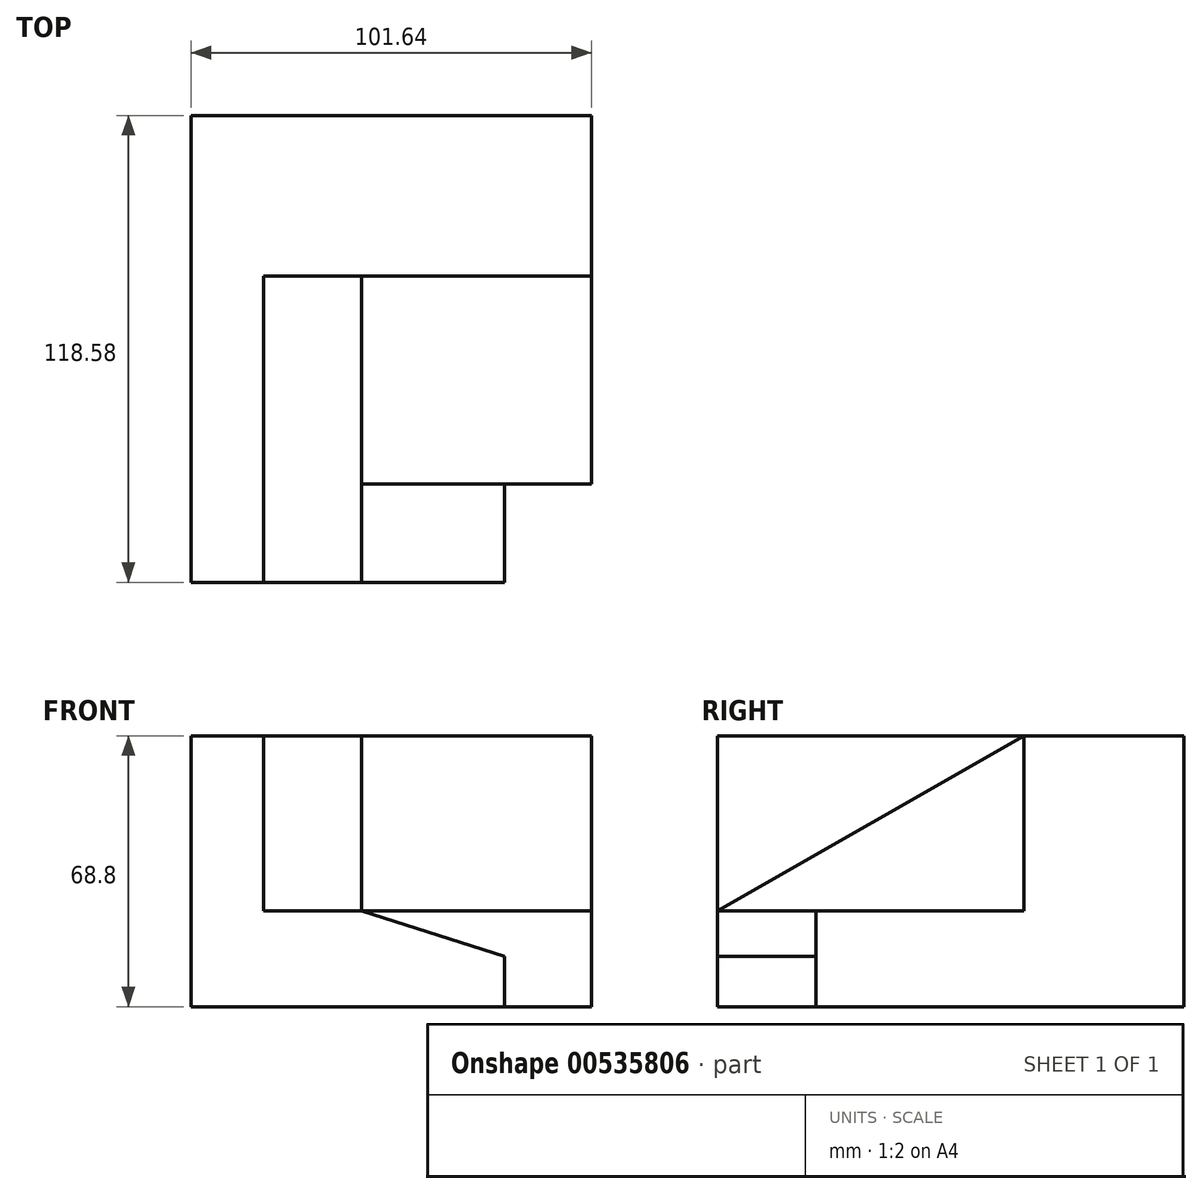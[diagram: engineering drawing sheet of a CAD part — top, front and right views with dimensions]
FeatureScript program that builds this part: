
annotation { "Feature Type Name" : "Feature", "Feature Type Description" : "" }
export const myFeature = defineFeature(function(context is Context, id is Id, definition is map)
    precondition{}
    {
        {
            var Q0;
            Q0=qCreatedBy(makeId("Top.planeOp"),FACE);
            var sketch = newSketch(context, id + "F0", { "sketchPlane" : qUnion([Q0])});
            skLineSegment(sketch, "E0.bottom", {"start": v(50.82, 59.3) * mm, "end": v(-50.82, 59.3) * mm});
            skLineSegment(sketch, "E0.top", {"start": v(-32.5, -59.3) * mm, "end": v(-50.82, -59.3) * mm});
            skLineSegment(sketch, "E0.left", {"start": v(50.82, 59.3) * mm, "end": v(50.82, 18.54) * mm});
            skLineSegment(sketch, "E0.right", {"start": v(-50.82, 59.3) * mm, "end": v(-50.82, -59.3) * mm});
            skPoint(sketch, "E0.middle", {"position": v(0, 0) * mm});
            skLineSegment(sketch, "E1.top", {"start": v(50.82, 18.54) * mm, "end": v(-32.5, 18.54) * mm});
            skLineSegment(sketch, "E1.right", {"start": v(-32.5, -59.3) * mm, "end": v(-32.5, 18.54) * mm});
            skSolve(sketch);
        }
        {
            var Q0;
            Q0=makeQuery(id+"F0.imprint","IMPRINT",FACE,{"disambiguationData":[TD([[makeQuery(id+"F0.imprint","IMPRINT",EDGE,{"derivedFrom":sQuery(id+"F0.wireOp",EDGE,"E0.bottom")}),1.0]])]});
            extrude(context, id + "F1", {"entities" : qUnion([Q0]), "endBound" : BoundingType.SYMMETRIC, "depth" : 68.8 * mm, "offsetDistance" : 25 * mm});
        }
        {
            var Q0;
            Q0=makeQuery(id+"F1.opExtrude","CAP_FACE",FACE,{"disambiguationData":[OSD([sQuery(id+"F0.wireOp",EDGE,"E0.bottom"),sQuery(id+"F0.wireOp",EDGE,"E0.top"),sQuery(id+"F0.wireOp",EDGE,"E0.left"),sQuery(id+"F0.wireOp",EDGE,"E0.right"),sQuery(id+"F0.wireOp",EDGE,"E1.top"),sQuery(id+"F0.wireOp",EDGE,"E1.right")])],"isStart":true});
            var sketch = newSketch(context, id + "F2", { "sketchPlane" : qUnion([Q0])});
            skPoint(sketch, "E2.oppositeSnap0", {"position": v(-41.66, 59.3) * mm});
            skLineSegment(sketch, "E2.bottom", {"start": v(-32.5, -18.54) * mm, "end": v(50.82, -18.54) * mm});
            skLineSegment(sketch, "E2.top", {"start": v(-32.5, 59.3) * mm, "end": v(50.82, 59.3) * mm});
            skLineSegment(sketch, "E2.left", {"start": v(-32.5, -18.54) * mm, "end": v(-32.5, 59.3) * mm});
            skLineSegment(sketch, "E2.right", {"start": v(50.82, -18.54) * mm, "end": v(50.82, 59.3) * mm});
            skSolve(sketch);
        }
        {
            var Q0;
            Q0=makeQuery(id+"F2.imprint","IMPRINT",FACE,{"disambiguationData":[TD([[makeQuery(id+"F2.imprint","IMPRINT",EDGE,{"derivedFrom":sQuery(id+"F2.wireOp",EDGE,"E2.bottom")}),-1.0]])]});
            extrude(context, id + "F3", {"entities" : qUnion([Q0]), "operationType" : NewBodyOperationType.ADD, "oppositeDirection" : true, "depth" : 24.3 * mm, "offsetDistance" : 25 * mm});
        }
        {
            var Q0;
            Q0=makeQuery(id+"F1.opExtrude","SWEPT_FACE",FACE,{"disambiguationData":[OSD([sQuery(id+"F0.wireOp",EDGE,"E1.right")])]});
            var sketch = newSketch(context, id + "F4", { "sketchPlane" : qUnion([Q0])});
            skLineSegment(sketch, "E3", {"start": v(-59.3, -10.1) * mm, "end": v(18.54, 34.4) * mm});
            skLineSegment(sketch, "E4", {"start": v(18.54, 34.4) * mm, "end": v(18.54, -10.1) * mm});
            skLineSegment(sketch, "E5", {"start": v(18.54, -10.1) * mm, "end": v(-59.3, -10.1) * mm});
            skSolve(sketch);
        }
        {
            var Q0;
            Q0=makeQuery(id+"F4.imprint","IMPRINT",FACE,{"disambiguationData":[TD([[makeQuery(id+"F4.imprint","IMPRINT",EDGE,{"derivedFrom":sQuery(id+"F4.wireOp",EDGE,"E3")}),-1.0]])]});
            extrude(context, id + "F5", {"entities" : qUnion([Q0]), "operationType" : NewBodyOperationType.ADD, "depth" : 25 * mm, "offsetDistance" : 25 * mm});
        }
        {
            var Q0;
            Q0=makeQuery(id+"F3.boolean.opBoolean","MERGE",FACE,{"derivedFrom":[makeQuery(id+"F1.opExtrude","SWEPT_FACE",FACE,{"disambiguationData":[OSD([sQuery(id+"F0.wireOp",EDGE,"E0.top")])]}),makeQuery(id+"F3.opExtrude","SWEPT_FACE",FACE,{"disambiguationData":[OSD([sQuery(id+"F2.wireOp",EDGE,"E2.top")])]})]});
            var sketch = newSketch(context, id + "F6", { "sketchPlane" : qUnion([Q0])});
            skLineSegment(sketch, "E6", {"start": v(-7.5, -10.1) * mm, "end": v(28.69, -21.58) * mm});
            skLineSegment(sketch, "E7", {"start": v(28.69, -21.58) * mm, "end": v(28.69, -34.4) * mm});
            skLineSegment(sketch, "E8", {"start": v(28.69, -34.4) * mm, "end": v(50.82, -34.4) * mm});
            skLineSegment(sketch, "E9", {"start": v(50.82, -34.4) * mm, "end": v(50.82, -10.1) * mm});
            skLineSegment(sketch, "E10", {"start": v(50.82, -10.1) * mm, "end": v(-7.5, -10.1) * mm});
            skSolve(sketch);
        }
        {
            var Q0;
            Q0=makeQuery(id+"F6.imprint","IMPRINT",FACE,{"disambiguationData":[TD([[makeQuery(id+"F6.imprint","IMPRINT",EDGE,{"derivedFrom":sQuery(id+"F6.wireOp",EDGE,"E6")}),1.0]])]});
            extrude(context, id + "F7", {"entities" : qUnion([Q0]), "operationType" : NewBodyOperationType.REMOVE, "oppositeDirection" : true, "depth" : 25 * mm, "offsetDistance" : 25 * mm});
        }
    });
